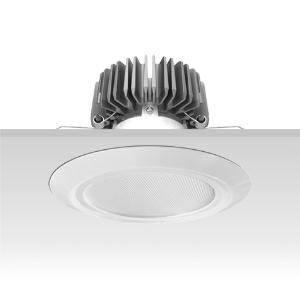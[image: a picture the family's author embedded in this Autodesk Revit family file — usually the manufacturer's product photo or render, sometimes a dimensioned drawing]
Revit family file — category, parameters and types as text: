
# Revit family: 3f_filippi_-_3f_reno_bianco_ampio_3f_filippi_-_30637_a01048_-_3f_reno_200_wh_4000-840_wide___smp_wh_9460
name_source: partatom
category: Lighting Fixtures
units: mm (PartAtom-declared; Revit-internal decimal feet)

## family parameters
Cut with Voids When Loaded = No
Host = Face
Light Source = No
Part Type = Normal
Room Calculation Point = No
Round Connector Dimension = Use Diameter
Shared = No

## types (1)
- 3F Filippi - 3F Reno Bianco Ampio (1 x LED, 3089 lm, 36 W, 4000 K)
    Apparent Load = 36 VA
    Approval mark = CE
    CIE Flux Codes = 74 92 98 100 100
    Color Rendering = 80
    Color Temperature = 4000 K
    Control Gear = Electronic ballast
    Default Elevation = 1800 mm
    Description = ILLUMINOTECHNICAL
Luminous efficiency 100% (DLOR 100%, ULOR 0%).
Initial luminous flux of the luminaire 3089 lm.
Direct symmetric wide distribution.
Installation Interdistance Transv.D = 1.06 x hu - Long.D = 1.04 x hu.
Tabular UGR (CIE 117 - 4H-8H; S=0.25H; 70/50/20): RUG 23.5 - 23.3.
Beam angle: 70° - 69°.
Luminous efficacy 86 lm/W.
Lifetime (L90/B10): 30000 h. (tq+25°C)
Lifetime (L85/B10): 50000 h. (tq+25°C)
Lifetime (L70/B10): 80000 h. (tq+25°C)
Sudden decreased luminous flux after 50000 hours: 0% (C0).
Photobiological safety in compliance with IEC/TR 62778: RG1 low risk, (IEC 62471).
In compliance with IEC/EN 62722-2-1 - IEC/EN 62717 standards.

SOURCE
Compact LED module 4000/840.
Energy efficiency class (UE 2019/2020 - UE 2019/2015): E.
CIE 13.3 Colour rendering index: CRI >80 (R9 <50%).
IES TM-30 Fidelity Index: Rf = 84 Rg = 95.
CCT nominal colour temperature 4000 K.
Colour initial tolerance (MacAdam): SDCM 3.
Zhaga Book 3 compliant.

MECHANICAL
Passive heat dissipator in die-casting aluminium, oversized, for optimum thermal management of the LED module.
Parabolic element with graduated/concentric rings in white polycarbonate.
Transparent external lens with glossy and satin differentiated surfaces, with a cooling and anti-insect system in methacrylate (PMMA).
Fastening spring clips in stainless steel.
Dimensions: diameter 226 mm, height 146 mm. Weight 1.655 kg.
IP44 protection degree for exposed part, IP20 for recessed part.
Mechanical strength to impacts IK05 (0.7 joule).
Glow-wire test resistance 650°C.

ELECTRICAL
Wiring on a separate unit.
Halogen Free electronic wiring 230V-50/60Hz, power factor 0.95, THD <25%, constant output current, SELV, class II, 1 driver.
Power of the luminaire 36 W.
ENEC - CE.
SAFE FLICKER: PstLM=<1 and SVM=<0.4 (IEC TR 61547-1 and IEC TR 63158), to ensure a more comfortable and safe light.
Luminaire compliant with EN 60598-2-22 for power supply from a centralised emergency system CPSS (Central Power Supply System), not incorporated in the luminaire - high risk areas excluded. The default power and flux are 100% in AC and 100% in DC.
Ambient temperature from 0°C to +25°C.
Temperature class T6 max 85°C.
Relative humidity UR: <85%.

INSTALLATION
Pull-up recessed fitting.
False ceiling carving: 200 mm.
All accessories dedicated to this product are available on the Catalog and on our website www.3F-Filippi.com.

ACCESSORIES
A01048 - Anti-glare microprismatic SMP diffuser in methacrylate (PMMA), locked and in line with the trim, in white polycarbonate.

APPLICATIONS
Suitable product for food production plants (HACCP), IFS (Food Version 6), BRC (GSFS Food Version 7).
Environments: architectural, commercial, exhibition areas, transit areas, corridors, shops, display windows, service areas.
In false ceilings with narrow voids.

WARNING
Luminaire designed for disposal/recycling at end-of-life.
Replaceable (LED only) light source by a professional. Replaceable control gear by a professional.
    Height = 0 mm  [stored 0 ft]
    Lamp = 1 x LED
    Lamp Light Flux = 3089 lm
    Lamp Power = 36 W
    Lamp count = 1
    Length = 226 mm
    Lifetime = 50000 h
    Luminous efficacy = 86 lm/W
    Manufacturer = 3F Filippi
    ModVariant = No
    Model = 3F Filippi - 30637+A01048 - 3F Reno 200 WH 4000-840 WIDE + SMP WH
    Mounting Place = Ceiling
    Mounting Type = Recessed
    Number of Poles = 1
    OnlyDefault = Yes
    Power Factor = 1
    Product Name = 3F Filippi - 3F Reno Bianco Ampio
    Product group = recessed luminaire
    ProductGroupID = 4
    Protection Class = Protection class II
    Protection Degree = IP 20
    RLX_Detail_Level = 1
    RLX_Emergency_Light_Flux = 0 lm
    RLX_Emergency_Type = 0
    RLX_Emergency_Type_DB = No
    RlxData = <blob elided: 94945 chars, md5=6a70ec57>
    Socket = socket
    Standby Power = 0 W
    System Light Flux = 3089 lm
    System Power = 36 W
    Type Comments = Product without accessories
    Type Image = 3ffilippi_3f_reno_200_wh_vs_smp.jpg
    URL = http://relux.com
    VarID = ---
    Voltage = 0 V
    Weight = 0.00 kg
    Width = 0 mm  [stored 0 ft]

note: [stored X ft] marks values corroborated as IEEE doubles in the binary element streams (Revit-internal decimal feet)

## geometry (parser evidence)
native form markers: Blend x4, Sweep x10
no freeform markers — native parametric forms only
